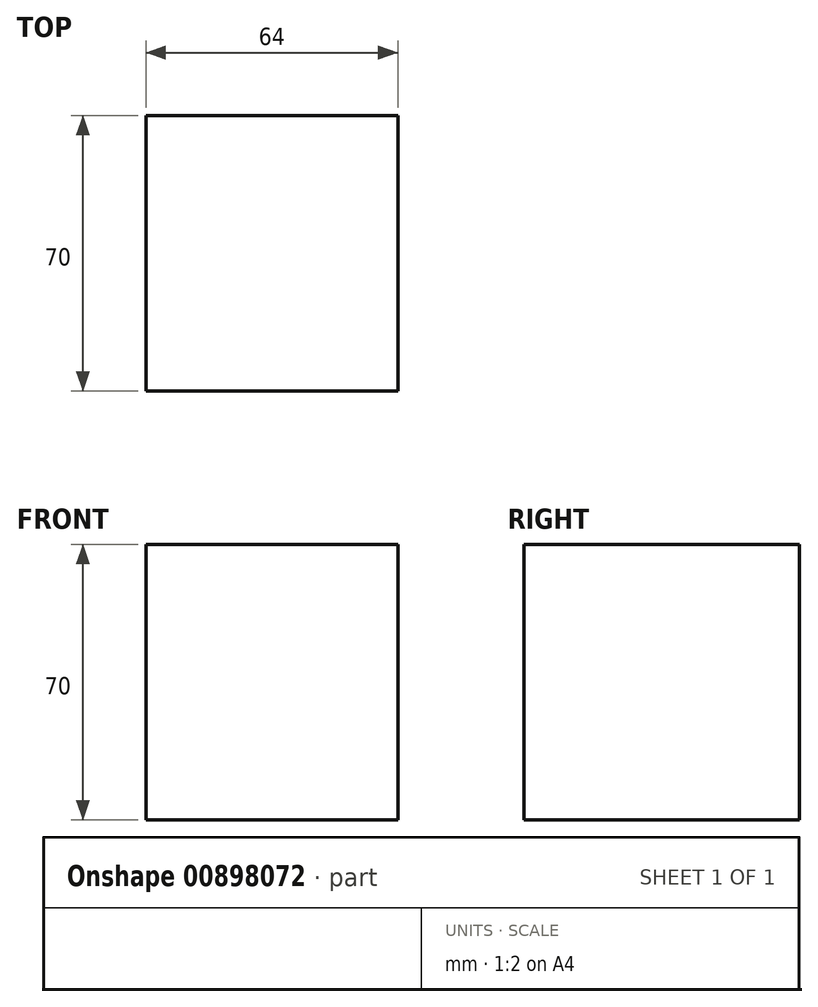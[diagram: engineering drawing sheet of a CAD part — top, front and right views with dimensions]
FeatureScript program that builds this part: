
annotation { "Feature Type Name" : "Feature", "Feature Type Description" : "" }
export const myFeature = defineFeature(function(context is Context, id is Id, definition is map)
    precondition{}
    {
        {
            var Q0;
            Q0=qCreatedBy(makeId("Top.planeOp"),FACE);
            var sketch = newSketch(context, id + "F0", { "sketchPlane" : qUnion([Q0])});
            skLineSegment(sketch, "E0.bottom", {"start": v(0, 0) * mm, "end": v(64, 0) * mm});
            skLineSegment(sketch, "E0.top", {"start": v(0, 70) * mm, "end": v(64, 70) * mm});
            skLineSegment(sketch, "E0.left", {"start": v(0, 0) * mm, "end": v(0, 70) * mm});
            skLineSegment(sketch, "E0.right", {"start": v(64, 0) * mm, "end": v(64, 70) * mm});
            skSolve(sketch);
        }
        {
            var Q0;
            Q0 = qSketchRegion(id + "F0", true);
            extrude(context, id + "F1", {"entities" : qUnion([Q0]), "depth" : 70 * mm, "offsetDistance" : 25 * mm});
        }
    });
